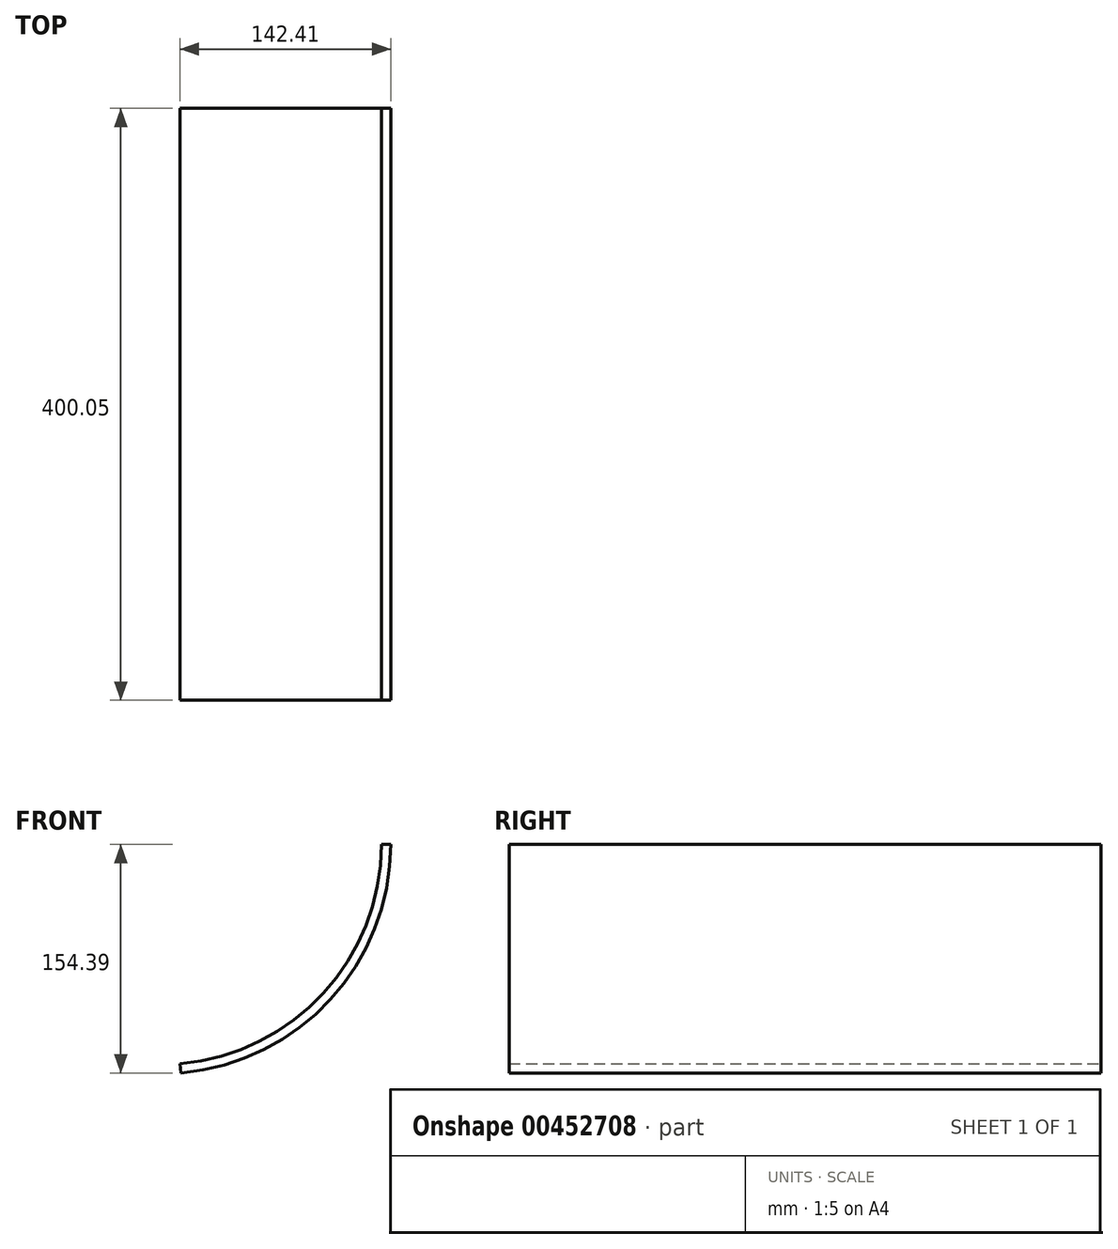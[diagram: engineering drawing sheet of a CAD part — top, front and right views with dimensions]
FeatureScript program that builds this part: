
annotation { "Feature Type Name" : "Feature", "Feature Type Description" : "" }
export const myFeature = defineFeature(function(context is Context, id is Id, definition is map)
    precondition{}
    {
        {
            var Q0;
            Q0=qCreatedBy(makeId("Front.planeOp"),FACE);
            var sketch = newSketch(context, id + "F0", { "sketchPlane" : qUnion([Q0])});
            skArc(sketch, "E0", {"start": v(0, -148.6) * mm, "mid": v(105.07, -105.07) * mm, "end": v(148.6, 0) * mm});
            skLineSegment(sketch, "E1", {"start": v(148.6, 0) * mm, "end": v(154.94, 0) * mm});
            skLineSegment(sketch, "E2", {"start": v(0, -148.6) * mm, "end": v(0, -154.94) * mm});
            skArc(sketch, "E3", {"start": v(0, -154.94) * mm, "mid": v(109.56, -109.56) * mm, "end": v(154.94, 0) * mm});
            skLineSegment(sketch, "E4", {"start": v(148.6, 0) * mm, "end": v(0, 0) * mm});
            skLineSegment(sketch, "E5", {"start": v(0, -4.79) * mm, "end": v(13.09, -154.39) * mm});
            skSolve(sketch);
        }
        {
            var Q0;
            {var subQ0=sQuery(id+"F0.wireOp",EDGE,"E1");Q0=makeQuery(id+"F0.imprint","IMPRINT",FACE,{"disambiguationData":[TD([[makeQuery(id+"F0.imprint","IMPRINT",EDGE,{"derivedFrom":subQ0}),-1.0]])]});}
            extrude(context, id + "F1", {"entities" : qUnion([Q0]), "depth" : 400.05 * mm, "offsetDistance" : 25.4 * mm});
        }
    });
